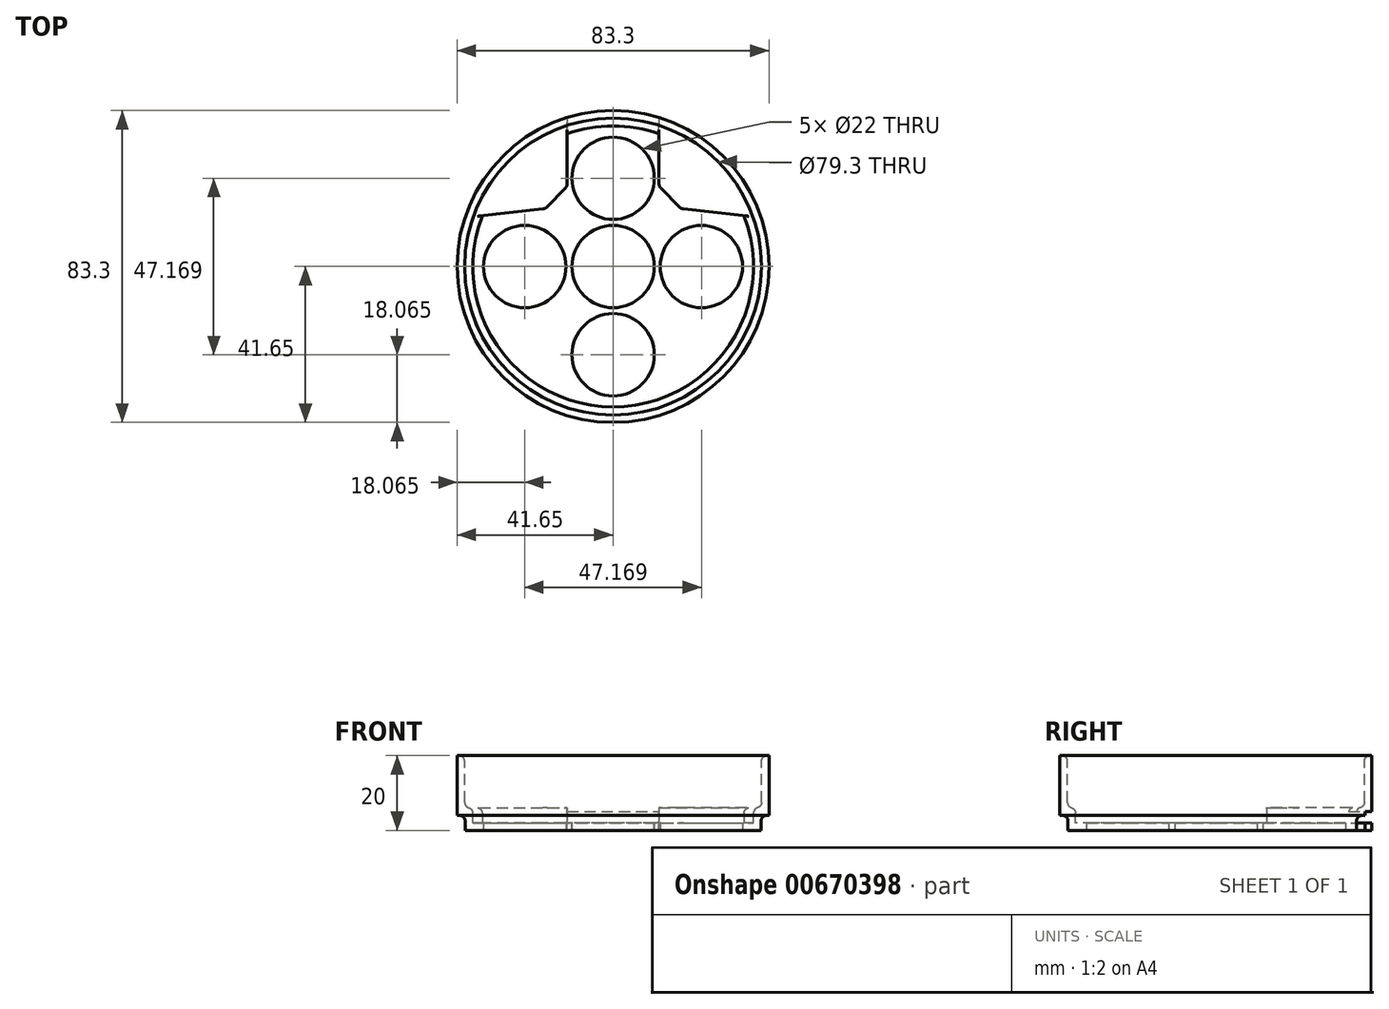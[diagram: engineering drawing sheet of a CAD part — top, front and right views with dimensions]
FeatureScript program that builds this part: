
annotation { "Feature Type Name" : "Feature", "Feature Type Description" : "" }
export const myFeature = defineFeature(function(context is Context, id is Id, definition is map)
    precondition{}
    {
        {
            var Q0;
            Q0=qCreatedBy(makeId("Front.planeOp"),FACE);
            var sketch = newSketch(context, id + "F0", { "sketchPlane" : qUnion([Q0])});
            skLineSegment(sketch, "E0", {"start": v(-37.5, 0) * mm, "end": v(-37.5, 4) * mm});
            skLineSegment(sketch, "E1", {"start": v(-39.5, 2) * mm, "end": v(-39.5, -2) * mm});
            skLineSegment(sketch, "E2", {"start": v(-37.5, 0) * mm, "end": v(0, 0) * mm});
            skLineSegment(sketch, "E3", {"start": v(-39.5, -2) * mm, "end": v(0, -2) * mm});
            skLineSegment(sketch, "E4", {"start": v(0, -2) * mm, "end": v(0, 0) * mm});
            skLineSegment(sketch, "E5", {"start": v(0, 21.98) * mm, "end": v(0, -26.9) * mm, "construction": true});
            skLineSegment(sketch, "E6", {"start": v(-39.5, 2) * mm, "end": v(-41.65, 2) * mm});
            skLineSegment(sketch, "E7", {"start": v(-41.65, 2) * mm, "end": v(-41.65, 18) * mm});
            skLineSegment(sketch, "E8", {"start": v(-41.65, 18) * mm, "end": v(-39.65, 18) * mm});
            skLineSegment(sketch, "E9", {"start": v(-39.65, 18) * mm, "end": v(-39.65, 4) * mm});
            skLineSegment(sketch, "E10", {"start": v(-39.65, 4) * mm, "end": v(-37.5, 4) * mm});
            skPoint(sketch, "E11.orphan", {"position": v(-37.5, 18) * mm});
            skSolve(sketch);
        }
        {
            var Q0;
            Q0=makeQuery(id+"F0.imprint","IMPRINT",FACE,{"disambiguationData":[TD([[makeQuery(id+"F0.imprint","IMPRINT",EDGE,{"derivedFrom":sQuery(id+"F0.wireOp",EDGE,"E0")}),1.0]])]});
            var Q1;
            {var subQ0=sQuery(id+"F0.wireOp",EDGE,"OWQfRE5u-Rv34-R4bg-iri2-STJ4Ix59SzPs");Q1=makeQuery(id+"F0.imprint","IMPRINT",FACE,{"disambiguationData":[TD([[makeQuery(id+"F0.imprint","IMPRINT",EDGE,{"derivedFrom":subQ0}),1.0]])]});}
            var Q2;
            Q2=sQuery(id+"F0.wireOp",EDGE,"E5");
            revolve(context, id + "F1", {"entities" : qUnion([Q0, Q1]), "axis" : qUnion([Q2]), "revolveType" : RevolveType.FULL});
        }
        {
            var Q0;
            {var subQ0=sQuery(id+"F0.wireOp",EDGE,"E3");Q0=makeQuery(id+"F1.opRevolve","SWEPT_FACE",FACE,{"disambiguationData":[OSD([subQ0]),TDD([makeQuery(id+"F0.imprint","IMPRINT",EDGE,{"disambiguationData":[TD([[makeQuery(id+"F0.imprint","INTERSECT",VERTEX,{"derivedFrom":[subQ0,sQuery(id+"F0.wireOp",EDGE,"E4")]}),1.0]])],"derivedFrom":subQ0})])]});}
            var sketch = newSketch(context, id + "F2", { "sketchPlane" : qUnion([Q0])});
            skCircle(sketch, "E12", {"center": v(0, 23.58) * mm, "radius": 11 * mm});
            skCircle(sketch, "E13.1.0", {"center": v(-23.58, 0) * mm, "radius": 11 * mm});
            skCircle(sketch, "E13.2.0", {"center": v(0, -23.58) * mm, "radius": 11 * mm});
            skCircle(sketch, "E13.3.0", {"center": v(23.58, 0) * mm, "radius": 11 * mm});
            skPoint(sketch, "E13.center", {"position": v(0, 0) * mm});
            skSolve(sketch);
        }
        {
            var Q0;
            Q0=makeQuery(id+"F2.imprint","IMPRINT",FACE,{"disambiguationData":[TD([[makeQuery(id+"F2.imprint","IMPRINT",EDGE,{"derivedFrom":sQuery(id+"F2.wireOp",EDGE,"E12")}),1.0]])]});
            var Q1;
            Q1=makeQuery(id+"F2.imprint","IMPRINT",FACE,{"disambiguationData":[TD([[makeQuery(id+"F2.imprint","IMPRINT",EDGE,{"derivedFrom":sQuery(id+"F2.wireOp",EDGE,"E13.1.0")}),1.0]])]});
            var Q2;
            Q2=makeQuery(id+"F2.imprint","IMPRINT",FACE,{"disambiguationData":[TD([[makeQuery(id+"F2.imprint","IMPRINT",EDGE,{"derivedFrom":sQuery(id+"F2.wireOp",EDGE,"E13.3.0")}),1.0]])]});
            var Q3;
            Q3=makeQuery(id+"F2.imprint","IMPRINT",FACE,{"disambiguationData":[TD([[makeQuery(id+"F2.imprint","IMPRINT",EDGE,{"derivedFrom":sQuery(id+"F2.wireOp",EDGE,"E13.2.0")}),1.0]])]});
            extrude(context, id + "F3", {"entities" : qUnion([Q0, Q1, Q2, Q3]), "operationType" : NewBodyOperationType.REMOVE, "oppositeDirection" : true, "depth" : 5 * mm, "offsetDistance" : 25 * mm});
        }
        {
            var Q0;
            Q0=makeQuery(id+"F1.opRevolve","SWEPT_EDGE",EDGE,{"disambiguationData":[OSD([sQuery(id+"F0.wireOp",EDGE,"E1"),sQuery(id+"F0.wireOp",EDGE,"E6")])]});
            var Q1;
            Q1=makeQuery(id+"F1.opRevolve","SWEPT_EDGE",EDGE,{"disambiguationData":[OSD([sQuery(id+"F0.wireOp",EDGE,"E9"),sQuery(id+"F0.wireOp",EDGE,"E10")])]});
            var Q2;
            Q2=makeQuery(id+"F1.opRevolve","SWEPT_EDGE",EDGE,{"disambiguationData":[OSD([sQuery(id+"F0.wireOp",EDGE,"E8"),sQuery(id+"F0.wireOp",EDGE,"E9")])]});
            fillet(context, id + "F4", {"entities" : qUnion([Q0, Q1, Q2]), "radius" : 1.5 * mm, "tangentPropagation" : true, "allowEdgeOverflow" : false});
        }
        {
            var Q0;
            Q0=makeQuery(id+"F2.imprint","IMPRINT",FACE,{"disambiguationData":[TD([[makeQuery(id+"F2.imprint","IMPRINT",EDGE,{"derivedFrom":sQuery(id+"F2.wireOp",EDGE,"E12")}),-1.0]])]});
            var sketch = newSketch(context, id + "F5", { "sketchPlane" : qUnion([Q0])});
            skLineSegment(sketch, "E14.bottom", {"start": v(12.25, -35) * mm, "end": v(-12.25, -35) * mm});
            skLineSegment(sketch, "E14.top", {"start": v(12.25, -43.76) * mm, "end": v(-12.25, -43.76) * mm});
            skLineSegment(sketch, "E14.left", {"start": v(12.25, -35) * mm, "end": v(12.25, -43.76) * mm});
            skLineSegment(sketch, "E14.right", {"start": v(-12.25, -35) * mm, "end": v(-12.25, -43.76) * mm});
            skPoint(sketch, "E14.middle", {"position": v(0, -39.38) * mm});
            skSolve(sketch);
        }
        {
            var Q0;
            {var subQ0=sQuery(id+"F5.wireOp",EDGE,"E14.bottom");Q0=makeQuery(id+"F5.imprint","IMPRINT",FACE,{"disambiguationData":[TD([[makeQuery(id+"F5.imprint","IMPRINT",EDGE,{"derivedFrom":subQ0}),1.0]])]});}
            var Q1;
            {var subQ0=sQuery(id+"F5.wireOp",EDGE,"E14.top");Q1=makeQuery(id+"F5.imprint","IMPRINT",FACE,{"disambiguationData":[TD([[makeQuery(id+"F5.imprint","IMPRINT",EDGE,{"derivedFrom":subQ0}),-1.0]])]});}
            extrude(context, id + "F6", {"entities" : qUnion([Q0, Q1]), "operationType" : NewBodyOperationType.REMOVE, "oppositeDirection" : true, "depth" : 5 * mm, "offsetDistance" : 25 * mm});
        }
        {
            var Q0;
            Q0=makeQuery(id+"F1.opRevolve","SWEPT_FACE",FACE,{"disambiguationData":[OSD([sQuery(id+"F0.wireOp",EDGE,"E2")])]});
            var sketch = newSketch(context, id + "F7", { "sketchPlane" : qUnion([Q0])});
            skLineSegment(sketch, "E15", {"start": v(-12.25, 35.44) * mm, "end": v(-12.25, 21.42) * mm});
            skLineSegment(sketch, "E16", {"start": v(-12.25, 21.42) * mm, "end": v(-18.12, 15.44) * mm});
            skLineSegment(sketch, "E17", {"start": v(-18.12, 15.44) * mm, "end": v(-34.96, 13.56) * mm});
            skLineSegment(sketch, "E18.MirrorCS", {"start": v(12.25, 35.44) * mm, "end": v(12.25, 21.42) * mm});
            skLineSegment(sketch, "E19.MirrorCS", {"start": v(12.25, 21.42) * mm, "end": v(18.12, 15.44) * mm});
            skLineSegment(sketch, "E20.MirrorCS", {"start": v(18.12, 15.44) * mm, "end": v(34.96, 13.56) * mm});
            skPoint(sketch, "E21.start.orphan", {"position": v(-29.97, 22.54) * mm});
            skPoint(sketch, "E22.MirrorCS.end.orphan", {"position": v(12.25, 35.44) * mm});
            skPoint(sketch, "E22.MirrorCS.start.orphan", {"position": v(29.97, 22.54) * mm});
            skSolve(sketch);
        }
        {
            var Q0;
            {var subQ5=sQuery(id+"F7.wireOp",EDGE,"E16");Q0=makeQuery(id+"F7.imprint","IMPRINT",FACE,{"disambiguationData":[TD([[makeQuery(id+"F7.imprint","IMPRINT",EDGE,{"derivedFrom":subQ5}),-1.0]])]});}
            var Q1;
            {var subQ1=sQuery(id+"F7.wireOp",EDGE,"E19.MirrorCS");Q1=makeQuery(id+"F7.imprint","IMPRINT",FACE,{"disambiguationData":[TD([[makeQuery(id+"F7.imprint","IMPRINT",EDGE,{"derivedFrom":subQ1}),1.0]])]});}
            var Q2;
            Q2=makeQuery(id+"F1.opRevolve","SWEPT_FACE",FACE,{"disambiguationData":[OSD([sQuery(id+"F0.wireOp",EDGE,"E10")])]});
            extrude(context, id + "F8", {"entities" : qUnion([Q0, Q1]), "operationType" : NewBodyOperationType.ADD, "endBound" : BoundingType.UP_TO_SURFACE, "depth" : 3 * mm, "endBoundEntityFace" : qUnion([Q2]), "offsetDistance" : 25 * mm});
        }
        {
            var Q0;
            Q0=makeQuery(id+"F8.boolean.opBoolean","SPLIT",EDGE,{"disambiguationData":[OD(1.0)],"derivedFrom":makeQuery(id+"F1.opRevolve","SWEPT_EDGE",EDGE,{"disambiguationData":[OSD([sQuery(id+"F0.wireOp",EDGE,"E0"),sQuery(id+"F0.wireOp",EDGE,"E10")])]})});
            var Q1;
            Q1=makeQuery(id+"F8.opExtrude","TWEAK_EDGE",EDGE,{"derivedFrom":[makeQuery(id+"F1.opRevolve","SWEPT_FACE",FACE,{"disambiguationData":[OSD([sQuery(id+"F0.wireOp",EDGE,"E10")])]}),makeQuery(id+"F7.imprint","IMPRINT",EDGE,{"derivedFrom":sQuery(id+"F7.wireOp",EDGE,"E21")})]});
            var Q2;
            Q2=makeQuery(id+"F8.opExtrude","TWEAK_EDGE",EDGE,{"derivedFrom":[makeQuery(id+"F1.opRevolve","SWEPT_FACE",FACE,{"disambiguationData":[OSD([sQuery(id+"F0.wireOp",EDGE,"E10")])]}),makeQuery(id+"F7.imprint","IMPRINT",EDGE,{"derivedFrom":sQuery(id+"F7.wireOp",EDGE,"E22.MirrorCS")})]});
            fillet(context, id + "F9", {"entities" : qUnion([Q0, Q1, Q2]), "radius" : 1.5 * mm, "tangentPropagation" : true, "allowEdgeOverflow" : false});
        }
        {
            var Q0;
            Q0=makeQuery(id+"F6.boolean.opBoolean","COPY",FACE,{"derivedFrom":makeQuery(id+"F6.opExtrude","SWEPT_FACE",FACE,{"disambiguationData":[OSD([sQuery(id+"F5.wireOp",EDGE,"E14.bottom")])]})});
            var Q1;
            Q1=makeQuery(id+"F1.opRevolve","SWEPT_FACE",FACE,{"disambiguationData":[OSD([sQuery(id+"F0.wireOp",EDGE,"E7")])]});
            extrude(context, id + "F10", {"entities" : qUnion([Q0]), "operationType" : NewBodyOperationType.ADD, "endBound" : BoundingType.UP_TO_SURFACE, "depth" : 9.1 * mm, "endBoundEntityFace" : qUnion([Q1]), "offsetDistance" : 25 * mm});
        }
        {
            var Q0;
            Q0=makeQuery(id+"F8.opExtrude","SWEPT_EDGE",EDGE,{"disambiguationData":[OSD([sQuery(id+"F7.wireOp",EDGE,"E15"),sQuery(id+"F7.wireOp",EDGE,"E16")])]});
            var Q1;
            Q1=makeQuery(id+"F8.opExtrude","SWEPT_EDGE",EDGE,{"disambiguationData":[OSD([sQuery(id+"F7.wireOp",EDGE,"E16"),sQuery(id+"F7.wireOp",EDGE,"E17")])]});
            var Q2;
            Q2=makeQuery(id+"F8.opExtrude","SWEPT_EDGE",EDGE,{"disambiguationData":[OSD([sQuery(id+"F0.wireOp",EDGE,"E0"),sQuery(id+"F0.wireOp",EDGE,"E2"),sQuery(id+"F7.wireOp",EDGE,"E17")])]});
            var Q3;
            Q3=makeQuery(id+"F8.opExtrude","SWEPT_EDGE",EDGE,{"disambiguationData":[OSD([sQuery(id+"F7.wireOp",EDGE,"E18.MirrorCS"),sQuery(id+"F7.wireOp",EDGE,"E19.MirrorCS")])]});
            var Q4;
            Q4=makeQuery(id+"F8.opExtrude","SWEPT_EDGE",EDGE,{"disambiguationData":[OSD([sQuery(id+"F7.wireOp",EDGE,"E19.MirrorCS"),sQuery(id+"F7.wireOp",EDGE,"E20.MirrorCS")])]});
            var Q5;
            Q5=makeQuery(id+"F8.opExtrude","SWEPT_EDGE",EDGE,{"disambiguationData":[OSD([sQuery(id+"F0.wireOp",EDGE,"E0"),sQuery(id+"F0.wireOp",EDGE,"E2"),sQuery(id+"F7.wireOp",EDGE,"E20.MirrorCS")])]});
            fillet(context, id + "F11", {"entities" : qUnion([Q0, Q1, Q2, Q3, Q4, Q5]), "radius" : 2 * mm, "tangentPropagation" : true, "allowEdgeOverflow" : false});
        }
        {
            var Q0;
            {var subQ0=sQuery(id+"F5.wireOp",EDGE,"E14.bottom");var subQ2=sQuery(id+"F0.wireOp",EDGE,"E2");var subQ3=makeQuery(id+"F1.opRevolve","SWEPT_FACE",FACE,{"disambiguationData":[OSD([subQ2])]});Q0=makeQuery(id+"F10.boolean.opBoolean","MERGE",FACE,{"derivedFrom":[subQ3,makeQuery(id+"F10.opExtrude","SWEPT_FACE",FACE,{"disambiguationData":[OSD([subQ2,subQ0]),TDD([makeQuery(id+"F6.boolean.opBoolean","INTERSECT",EDGE,{"derivedFrom":[subQ3,makeQuery(id+"F6.opExtrude","SWEPT_FACE",FACE,{"disambiguationData":[OSD([subQ0]),TDD([makeQuery(id+"F5.imprint","IMPRINT",EDGE,{"disambiguationData":[TD([[makeQuery(id+"F5.imprint","INTERSECT",VERTEX,{"derivedFrom":[subQ0,sQuery(id+"F5.wireOp",EDGE,"E14.left")]}),-1.0]])],"derivedFrom":subQ0})])]})]})])]}),makeQuery(id+"F10.opExtrude","SWEPT_FACE",FACE,{"disambiguationData":[OSD([subQ2,subQ0]),TDD([makeQuery(id+"F6.boolean.opBoolean","INTERSECT",EDGE,{"derivedFrom":[subQ3,makeQuery(id+"F6.opExtrude","SWEPT_FACE",FACE,{"disambiguationData":[OSD([subQ0]),TDD([makeQuery(id+"F5.imprint","IMPRINT",EDGE,{"disambiguationData":[TD([[makeQuery(id+"F5.imprint","INTERSECT",VERTEX,{"derivedFrom":[subQ0,sQuery(id+"F5.wireOp",EDGE,"E14.right")]}),1.0]])],"derivedFrom":subQ0})])]})]})])]})]});}
            var sketch = newSketch(context, id + "F12", { "sketchPlane" : qUnion([Q0])});
            skCircle(sketch, "E23", {"center": v(0, 0) * mm, "radius": 11 * mm});
            skSolve(sketch);
        }
        {
            var Q0;
            Q0=makeQuery(id+"F12.imprint","IMPRINT",FACE,{"disambiguationData":[TD([[makeQuery(id+"F12.imprint","IMPRINT",EDGE,{"derivedFrom":sQuery(id+"F12.wireOp",EDGE,"E23")}),1.0]])]});
            var Q1;
            {var subQ0=sQuery(id+"F5.wireOp",EDGE,"E14.bottom");Q1=makeQuery(id+"F10.boolean.opBoolean","MERGE",FACE,{"derivedFrom":[makeQuery(id+"F1.opRevolve","SWEPT_FACE",FACE,{"disambiguationData":[OSD([sQuery(id+"F0.wireOp",EDGE,"E3")])]}),makeQuery(id+"F10.opExtrude","SWEPT_FACE",FACE,{"disambiguationData":[OSD([subQ0]),TDD([makeQuery(id+"F6.boolean.opBoolean","COPY",EDGE,{"derivedFrom":makeQuery(id+"F6.opExtrude","CAP_EDGE",EDGE,{"disambiguationData":[OSD([subQ0]),TDD([makeQuery(id+"F5.imprint","IMPRINT",EDGE,{"disambiguationData":[TD([[makeQuery(id+"F5.imprint","INTERSECT",VERTEX,{"derivedFrom":[subQ0,sQuery(id+"F5.wireOp",EDGE,"E14.left")]}),-1.0]])],"derivedFrom":subQ0})])],"isStart":true})})])]}),makeQuery(id+"F10.opExtrude","SWEPT_FACE",FACE,{"disambiguationData":[OSD([subQ0]),TDD([makeQuery(id+"F6.boolean.opBoolean","COPY",EDGE,{"derivedFrom":makeQuery(id+"F6.opExtrude","CAP_EDGE",EDGE,{"disambiguationData":[OSD([subQ0]),TDD([makeQuery(id+"F5.imprint","IMPRINT",EDGE,{"disambiguationData":[TD([[makeQuery(id+"F5.imprint","INTERSECT",VERTEX,{"derivedFrom":[subQ0,sQuery(id+"F5.wireOp",EDGE,"E14.right")]}),1.0]])],"derivedFrom":subQ0})])],"isStart":true})})])]})]});}
            extrude(context, id + "F13", {"entities" : qUnion([Q0]), "operationType" : NewBodyOperationType.REMOVE, "endBound" : BoundingType.UP_TO_SURFACE, "oppositeDirection" : true, "depth" : 25 * mm, "endBoundEntityFace" : qUnion([Q1]), "offsetDistance" : 25 * mm});
        }
    });
